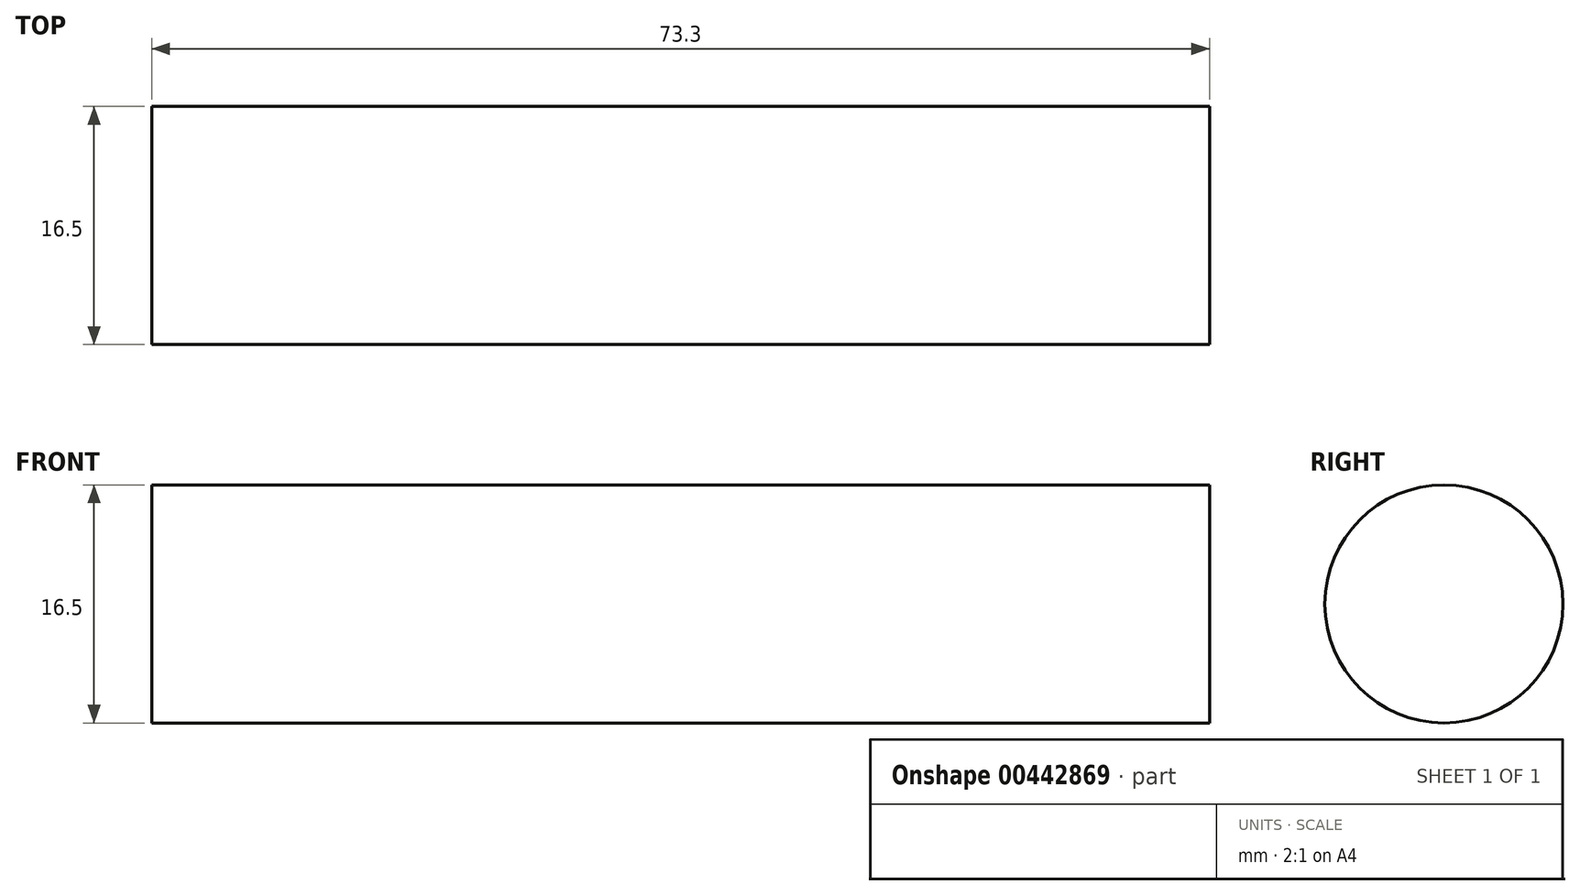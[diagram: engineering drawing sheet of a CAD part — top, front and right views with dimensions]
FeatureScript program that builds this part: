
annotation { "Feature Type Name" : "Feature", "Feature Type Description" : "" }
export const myFeature = defineFeature(function(context is Context, id is Id, definition is map)
    precondition{}
    {
        {
            var Q0;
            Q0=qCreatedBy(makeId("Right.planeOp"),FACE);
            var sketch = newSketch(context, id + "F0", { "sketchPlane" : qUnion([Q0])});
            skCircle(sketch, "E0", {"center": v(0, 0) * mm, "radius": 8.25 * mm});
            skSolve(sketch);
        }
        {
            var Q0;
            Q0 = qSketchRegion(id + "F0", true);
            extrude(context, id + "F1", {"entities" : qUnion([Q0]), "depth" : 73.3 * mm});
        }
    });
